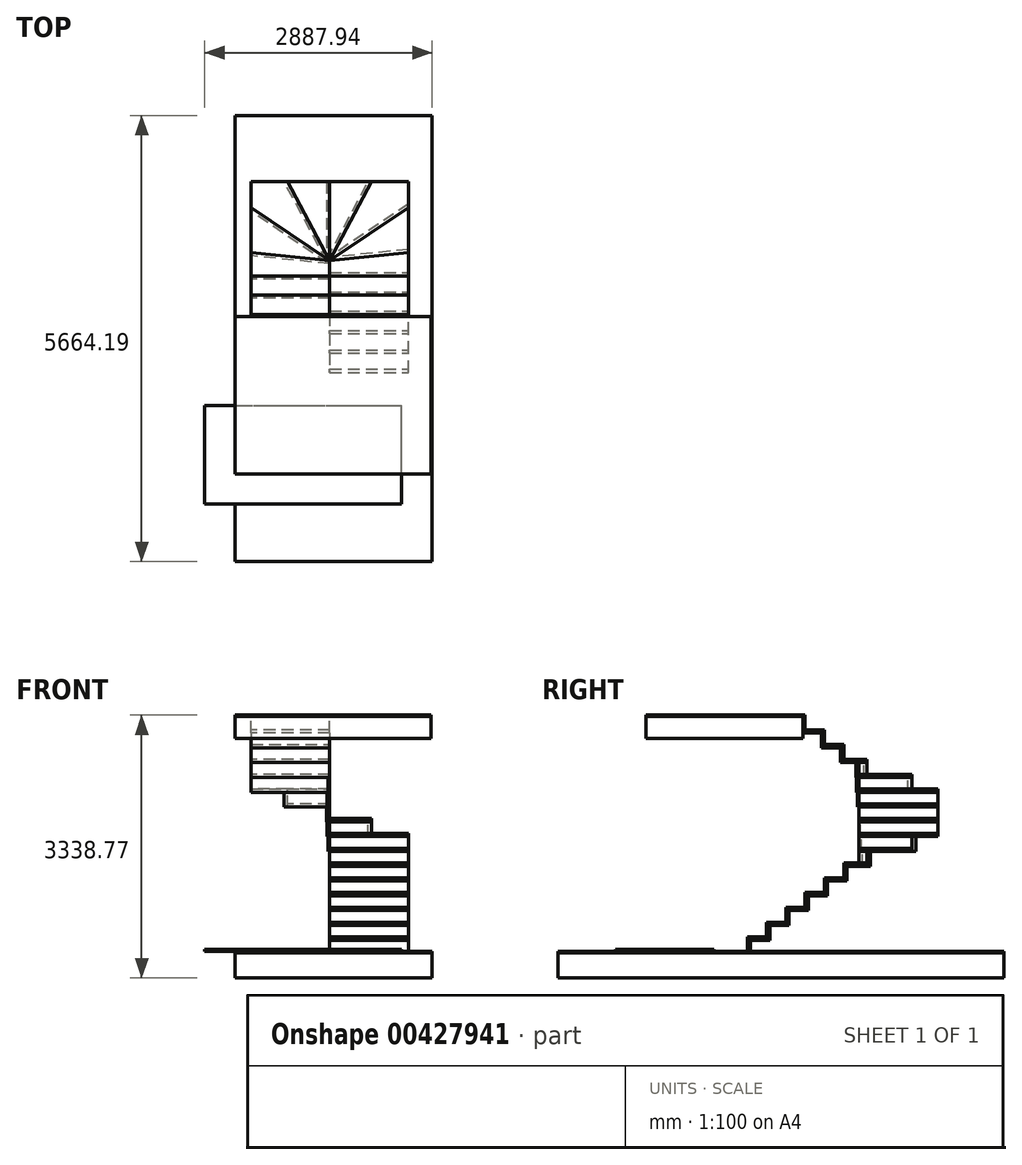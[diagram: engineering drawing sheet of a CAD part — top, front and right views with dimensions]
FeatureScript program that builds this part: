
annotation { "Feature Type Name" : "Feature", "Feature Type Description" : "" }
export const myFeature = defineFeature(function(context is Context, id is Id, definition is map)
    precondition{}
    {
        {
            assignVariable(context, id + "F0", {"name" : "up", "anyValue" : 188 - 40});
        }
        {
            assignVariable(context, id + "F1", {"name" : "height", "anyValue" : 188});
        }
        {
            var Q0;
            Q0=qCreatedBy(makeId("Top.planeOp"),FACE);
            var sketch = newSketch(context, id + "F2", { "sketchPlane" : qUnion([Q0])});
            skLineSegment(sketch, "E0.bottom", {"start": v(1000, 855) * mm, "end": v(-1000, 855) * mm, "construction": true});
            skLineSegment(sketch, "E0.top", {"start": v(1000, -855) * mm, "end": v(-1000, -855) * mm, "construction": true});
            skLineSegment(sketch, "E0.left", {"start": v(1000, 855) * mm, "end": v(1000, -855) * mm});
            skLineSegment(sketch, "E0.right", {"start": v(-1000, 855) * mm, "end": v(-1000, -855) * mm, "construction": true});
            skPoint(sketch, "E0.middle", {"position": v(0, 0) * mm});
            skLineSegment(sketch, "E1.bottom", {"start": v(-1000, -855) * mm, "end": v(0, -855) * mm, "construction": true});
            skLineSegment(sketch, "E1.top", {"start": v(-1000, 855) * mm, "end": v(0, 855) * mm, "construction": true});
            skLineSegment(sketch, "E1.left", {"start": v(-1000, -855) * mm, "end": v(-1000, 855) * mm});
            skLineSegment(sketch, "E1.right", {"start": v(0, -855) * mm, "end": v(0, 855) * mm});
            skLineSegment(sketch, "E2.bottom", {"start": v(1000, -855) * mm, "end": v(0, -855) * mm, "construction": true});
            skLineSegment(sketch, "E2.top", {"start": v(1000, 855) * mm, "end": v(0, 855) * mm});
            skLineSegment(sketch, "E2.left", {"start": v(1000, -855) * mm, "end": v(1000, 855) * mm});
            skLineSegment(sketch, "E3.bottom", {"start": v(-1000, 855) * mm, "end": v(1000, 855) * mm});
            skLineSegment(sketch, "E3.top", {"start": v(-1000, -145) * mm, "end": v(1000, -145) * mm, "construction": true});
            skLineSegment(sketch, "E3.left", {"start": v(-1000, 855) * mm, "end": v(-1000, -145) * mm, "construction": true});
            skLineSegment(sketch, "E3.right", {"start": v(1000, 855) * mm, "end": v(1000, -145) * mm, "construction": true});
            skCircle(sketch, "E4", {"center": v(0, -145) * mm, "radius": 1000 * mm, "construction": true});
            skArc(sketch, "E5", {"start": v(0, 355) * mm, "mid": v(-121.28, 340.07) * mm, "end": v(-235.31, 296.17) * mm, "construction": true});
            skArc(sketch, "E6", {"start": v(-235.31, 296.17) * mm, "mid": v(-335.3, 225.92) * mm, "end": v(-415.25, 133.51) * mm, "construction": true});
            skArc(sketch, "E7", {"start": v(-415.25, 133.51) * mm, "mid": v(-470.4, 24.47) * mm, "end": v(-497.46, -94.69) * mm, "construction": true});
            skArc(sketch, "E8", {"start": v(-497.46, -94.69) * mm, "mid": v(-499.37, -119.81) * mm, "end": v(-500, -145) * mm, "construction": true});
            skLineSegment(sketch, "E9", {"start": v(-500, -145) * mm, "end": v(-500, -855) * mm, "construction": true});
            skLineSegment(sketch, "E10", {"start": v(-1000, -340) * mm, "end": v(0, -340) * mm});
            skLineSegment(sketch, "E11", {"start": v(0, -585) * mm, "end": v(-1000, -585) * mm});
            skLineSegment(sketch, "E12", {"start": v(0, -830) * mm, "end": v(-1000, -830) * mm});
            skArc(sketch, "E13", {"start": v(0, 355) * mm, "mid": v(121.28, 340.07) * mm, "end": v(235.31, 296.17) * mm, "construction": true});
            skArc(sketch, "E14", {"start": v(235.31, 296.17) * mm, "mid": v(335.3, 225.92) * mm, "end": v(415.25, 133.51) * mm, "construction": true});
            skArc(sketch, "E15", {"start": v(415.25, 133.51) * mm, "mid": v(470.4, 24.47) * mm, "end": v(497.46, -94.69) * mm, "construction": true});
            skArc(sketch, "E16", {"start": v(497.46, -94.69) * mm, "mid": v(499.37, -119.81) * mm, "end": v(500, -145) * mm, "construction": true});
            skLineSegment(sketch, "E17", {"start": v(0, -340) * mm, "end": v(1000, -340) * mm});
            skLineSegment(sketch, "E18", {"start": v(0, -585) * mm, "end": v(1000, -585) * mm});
            skLineSegment(sketch, "E19", {"start": v(0, -830) * mm, "end": v(1000, -830) * mm});
            skLineSegment(sketch, "E20", {"start": v(0, -855) * mm, "end": v(0, -2275) * mm});
            skLineSegment(sketch, "E21", {"start": v(0, -2275) * mm, "end": v(1000, -2275) * mm});
            skLineSegment(sketch, "E22", {"start": v(1000, -2275) * mm, "end": v(1000, -855) * mm});
            skLineSegment(sketch, "E23", {"start": v(0, -145) * mm, "end": v(-497.46, -94.69) * mm});
            skLineSegment(sketch, "E24", {"start": v(-497.46, -94.69) * mm, "end": v(-1000, -43.86) * mm});
            skPoint(sketch, "E24.endSnap0", {"position": v(-1000, 0) * mm});
            skLineSegment(sketch, "E25", {"start": v(0, -145) * mm, "end": v(-415.25, 133.51) * mm});
            skLineSegment(sketch, "E26", {"start": v(-415.25, 133.51) * mm, "end": v(-1000, 525.7) * mm});
            skLineSegment(sketch, "E27", {"start": v(0, -145) * mm, "end": v(-235.31, 296.17) * mm});
            skLineSegment(sketch, "E28", {"start": v(-235.31, 296.17) * mm, "end": v(-533.39, 855) * mm});
            skLineSegment(sketch, "E29", {"start": v(0, -145) * mm, "end": v(235.31, 296.17) * mm});
            skLineSegment(sketch, "E30", {"start": v(235.31, 296.17) * mm, "end": v(533.39, 855) * mm});
            skLineSegment(sketch, "E31", {"start": v(0, -145) * mm, "end": v(415.25, 133.51) * mm});
            skLineSegment(sketch, "E32", {"start": v(415.25, 133.51) * mm, "end": v(1000, 525.7) * mm});
            skLineSegment(sketch, "E33", {"start": v(0, -145) * mm, "end": v(497.46, -94.69) * mm});
            skLineSegment(sketch, "E34", {"start": v(497.46, -94.69) * mm, "end": v(1000, -43.86) * mm});
            skLineSegment(sketch, "E35", {"start": v(0, -1075) * mm, "end": v(1000, -1075) * mm});
            skLineSegment(sketch, "E36", {"start": v(0, -1320) * mm, "end": v(1000, -1320) * mm});
            skLineSegment(sketch, "E37", {"start": v(0, -1565) * mm, "end": v(1000, -1565) * mm});
            skSolve(sketch);
        }
        {
            var Q0;
            Q0=qCreatedBy(makeId("Front.planeOp"),FACE);
            var Q1;
            Q1=sQuery(id+"F2.wireOp",VERTEX,"E1.right.start");
            cPlane(context, id + "F3", {"entities" : qUnion([Q0, Q1]), "cplaneType" : CPlaneType.PLANE_POINT, "offset" : 25 * mm, "width" : 150 * mm, "height" : 150 * mm});
        }
        {
            var Q0;
            Q0=qCreatedBy(id+"F3.planeOp",FACE);
            var sketch = newSketch(context, id + "F4", { "sketchPlane" : qUnion([Q0])});
            skLineSegment(sketch, "E38.bottom", {"start": v(-1199.88, 172) * mm, "end": v(1286.42, 172) * mm});
            skLineSegment(sketch, "E38.top", {"start": v(-1199.88, -108) * mm, "end": v(1286.42, -108) * mm});
            skLineSegment(sketch, "E38.left", {"start": v(-1199.88, 172) * mm, "end": v(-1199.88, -108) * mm});
            skLineSegment(sketch, "E38.right", {"start": v(1286.42, 172) * mm, "end": v(1286.42, -108) * mm});
            skSolve(sketch);
        }
        {
            var Q0;
            Q0 = qSketchRegion(id + "F4", true);
            extrude(context, id + "F5", {"entities" : qUnion([Q0]), "depth" : 2000 * mm});
        }
        {
            var Q0;
            Q0=makeQuery(id+"F5.opExtrude","SWEPT_FACE",FACE,{"disambiguationData":[OSD([sQuery(id+"F4.wireOp",EDGE,"E38.bottom")])]});
            extrude(context, id + "F6", {"entities" : qUnion([Q0]), "depth" : 16 * mm});
        }
        {
            var Q0;
            Q0=makeQuery(id+"F5.opExtrude","SWEPT_FACE",FACE,{"disambiguationData":[OSD([sQuery(id+"F4.wireOp",EDGE,"E38.left")])]});
            var sketch = newSketch(context, id + "F7", { "sketchPlane" : qUnion([Q0])});
            skLineSegment(sketch, "E39.bottom", {"start": v(3968.98, -3150.77) * mm, "end": v(-1695.2, -3150.77) * mm});
            skLineSegment(sketch, "E39.top", {"start": v(3968.98, -2833) * mm, "end": v(-1695.2, -2833) * mm});
            skLineSegment(sketch, "E39.left", {"start": v(3968.98, -3150.77) * mm, "end": v(3968.98, -2833) * mm});
            skLineSegment(sketch, "E39.right", {"start": v(-1695.2, -3150.77) * mm, "end": v(-1695.2, -2833) * mm});
            skLineSegment(sketch, "E40.0.0", {"start": v(855, 172) * mm, "end": v(855, -108) * mm});
            skLineSegment(sketch, "E40.0.1", {"start": v(855, -108) * mm, "end": v(2855, -108) * mm});
            skLineSegment(sketch, "E40.0.2", {"start": v(2855, -108) * mm, "end": v(2855, 172) * mm});
            skLineSegment(sketch, "E40.0.3", {"start": v(2855, 172) * mm, "end": v(855, 172) * mm});
            skSolve(sketch);
        }
        {
            var Q0;
            Q0=makeQuery(id+"F7.imprint","IMPRINT",FACE,{"disambiguationData":[TD([[makeQuery(id+"F7.imprint","IMPRINT",EDGE,{"derivedFrom":sQuery(id+"F7.wireOp",EDGE,"E39.bottom")}),-1.0]])]});
            extrude(context, id + "F8", {"entities" : qUnion([Q0]), "oppositeDirection" : true, "depth" : 2500 * mm});
        }
        {
            var Q0;
            Q0=makeQuery(id+"F8.opExtrude","SWEPT_FACE",FACE,{"disambiguationData":[OSD([sQuery(id+"F7.wireOp",EDGE,"E39.top")])]});
            extrude(context, id + "F9", {"entities" : qUnion([Q0]), "depth" : 16 * mm, "offsetDistance" : 25 * mm});
        }
        {
            var Q0;
            {var subQ0=sQuery(id+"F2.wireOp",EDGE,"E11");Q0=makeQuery(id+"F2.imprint","IMPRINT",FACE,{"disambiguationData":[TD([[makeQuery(id+"F2.imprint","IMPRINT",EDGE,{"derivedFrom":subQ0}),1.0]])]});}
            extrude(context, id + "F10", {"entities" : qUnion([Q0]), "oppositeDirection" : true, "depth" : 40 * mm});
        }
        {
            var Q0;
            Q0=makeQuery(id+"F10.opExtrude","CAP_FACE",FACE,{"disambiguationData":[OSD([sQuery(id+"F2.wireOp",EDGE,"E1.left"),sQuery(id+"F2.wireOp",EDGE,"E1.right"),sQuery(id+"F2.wireOp",EDGE,"E11"),sQuery(id+"F2.wireOp",EDGE,"E12")])],"isStart":false});
            cPlane(context, id + "F11", {"entities" : qUnion([Q0]), "cplaneType" : CPlaneType.OFFSET, "offset" : (getVariable(context, 'up')) * mm, "width" : 150 * mm, "height" : 150 * mm});
        }
        {
            var Q0;
            Q0=qCreatedBy(id+"F11.planeOp",FACE);
            var sketch = newSketch(context, id + "F12", { "sketchPlane" : qUnion([Q0])});
            skLineSegment(sketch, "E41.0.0", {"start": v(-1000, 585) * mm, "end": v(0, 585) * mm});
            skLineSegment(sketch, "E41.0.1", {"start": v(0, 585) * mm, "end": v(0, 340) * mm});
            skLineSegment(sketch, "E41.0.2", {"start": v(0, 340) * mm, "end": v(-1000, 340) * mm});
            skLineSegment(sketch, "E41.0.3", {"start": v(-1000, 340) * mm, "end": v(-1000, 585) * mm});
            skSolve(sketch);
        }
        {
            var Q0;
            Q0=makeQuery(id+"F12.imprint","IMPRINT",FACE,{"disambiguationData":[TD([[makeQuery(id+"F12.imprint","IMPRINT",EDGE,{"derivedFrom":sQuery(id+"F12.wireOp",EDGE,"E41.0.0")}),-1.0]])]});
            extrude(context, id + "F13", {"entities" : qUnion([Q0]), "depth" : 40 * mm});
        }
        {
            var Q0;
            Q0=makeQuery(id+"F13.opExtrude","CAP_FACE",FACE,{"disambiguationData":[OSD([sQuery(id+"F12.wireOp",EDGE,"E41.0.0"),sQuery(id+"F12.wireOp",EDGE,"E41.0.1"),sQuery(id+"F12.wireOp",EDGE,"E41.0.2"),sQuery(id+"F12.wireOp",EDGE,"E41.0.3")])],"isStart":false});
            cPlane(context, id + "F14", {"entities" : qUnion([Q0]), "cplaneType" : CPlaneType.OFFSET, "offset" : (getVariable(context, 'up')) * mm, "width" : 150 * mm, "height" : 150 * mm});
        }
        {
            var Q0;
            Q0=qCreatedBy(id+"F14.planeOp",FACE);
            var sketch = newSketch(context, id + "F15", { "sketchPlane" : qUnion([Q0])});
            skLineSegment(sketch, "E42.0.0", {"start": v(-1000, 43.86) * mm, "end": v(-1000, 340) * mm});
            skLineSegment(sketch, "E42.0.1", {"start": v(-1000, 340) * mm, "end": v(0, 340) * mm});
            skLineSegment(sketch, "E42.0.2", {"start": v(0, 340) * mm, "end": v(0, 145) * mm});
            skLineSegment(sketch, "E42.0.3", {"start": v(0, 145) * mm, "end": v(-497.46, 94.69) * mm});
            skLineSegment(sketch, "E42.0.4", {"start": v(-497.46, 94.69) * mm, "end": v(-1000, 43.86) * mm});
            skSolve(sketch);
        }
        {
            var Q0;
            Q0=makeQuery(id+"F15.imprint","IMPRINT",FACE,{"disambiguationData":[TD([[makeQuery(id+"F15.imprint","IMPRINT",EDGE,{"derivedFrom":sQuery(id+"F15.wireOp",EDGE,"E42.0.0")}),-1.0]])]});
            extrude(context, id + "F16", {"entities" : qUnion([Q0]), "depth" : 40 * mm});
        }
        {
            var Q0;
            Q0=makeQuery(id+"F16.opExtrude","CAP_FACE",FACE,{"disambiguationData":[OSD([sQuery(id+"F15.wireOp",EDGE,"E42.0.0"),sQuery(id+"F15.wireOp",EDGE,"E42.0.1"),sQuery(id+"F15.wireOp",EDGE,"E42.0.2"),sQuery(id+"F15.wireOp",EDGE,"E42.0.3"),sQuery(id+"F15.wireOp",EDGE,"E42.0.4")])],"isStart":false});
            cPlane(context, id + "F17", {"entities" : qUnion([Q0]), "cplaneType" : CPlaneType.OFFSET, "offset" : (getVariable(context, 'up')) * mm, "width" : 150 * mm, "height" : 150 * mm});
        }
        {
            var Q0;
            Q0=qCreatedBy(id+"F17.planeOp",FACE);
            var sketch = newSketch(context, id + "F18", { "sketchPlane" : qUnion([Q0])});
            skLineSegment(sketch, "E43.0.0", {"start": v(0, 145) * mm, "end": v(-415.25, -133.51) * mm});
            skLineSegment(sketch, "E43.0.1", {"start": v(-415.25, -133.51) * mm, "end": v(-1000, -525.7) * mm});
            skLineSegment(sketch, "E43.0.2", {"start": v(-1000, -525.7) * mm, "end": v(-1000, 43.86) * mm});
            skLineSegment(sketch, "E43.0.3", {"start": v(-1000, 43.86) * mm, "end": v(-497.46, 94.69) * mm});
            skLineSegment(sketch, "E43.0.4", {"start": v(-497.46, 94.69) * mm, "end": v(0, 145) * mm});
            skSolve(sketch);
        }
        {
            var Q0;
            Q0=makeQuery(id+"F18.imprint","IMPRINT",FACE,{"disambiguationData":[TD([[makeQuery(id+"F18.imprint","IMPRINT",EDGE,{"derivedFrom":sQuery(id+"F18.wireOp",EDGE,"E43.0.0")}),-1.0]])]});
            extrude(context, id + "F19", {"entities" : qUnion([Q0]), "depth" : 40 * mm});
        }
        {
            var Q0;
            Q0=makeQuery(id+"F19.opExtrude","CAP_FACE",FACE,{"disambiguationData":[OSD([sQuery(id+"F18.wireOp",EDGE,"E43.0.0"),sQuery(id+"F18.wireOp",EDGE,"E43.0.1"),sQuery(id+"F18.wireOp",EDGE,"E43.0.2"),sQuery(id+"F18.wireOp",EDGE,"E43.0.3"),sQuery(id+"F18.wireOp",EDGE,"E43.0.4")])],"isStart":false});
            cPlane(context, id + "F20", {"entities" : qUnion([Q0]), "cplaneType" : CPlaneType.OFFSET, "offset" : (getVariable(context, 'up')) * mm, "width" : 150 * mm, "height" : 150 * mm});
        }
        {
            var Q0;
            Q0=qCreatedBy(id+"F20.planeOp",FACE);
            var sketch = newSketch(context, id + "F21", { "sketchPlane" : qUnion([Q0])});
            skLineSegment(sketch, "E44.0.0", {"start": v(-1000, -525.7) * mm, "end": v(-415.25, -133.51) * mm});
            skLineSegment(sketch, "E44.0.1", {"start": v(-415.25, -133.51) * mm, "end": v(0, 145) * mm});
            skLineSegment(sketch, "E44.0.2", {"start": v(0, 145) * mm, "end": v(-235.31, -296.17) * mm});
            skLineSegment(sketch, "E44.0.3", {"start": v(-235.31, -296.17) * mm, "end": v(-533.39, -855) * mm});
            skLineSegment(sketch, "E44.0.4", {"start": v(-533.39, -855) * mm, "end": v(-1000, -855) * mm});
            skLineSegment(sketch, "E44.0.5", {"start": v(-1000, -855) * mm, "end": v(-1000, -525.7) * mm});
            skSolve(sketch);
        }
        {
            var Q0;
            Q0=makeQuery(id+"F21.imprint","IMPRINT",FACE,{"disambiguationData":[TD([[makeQuery(id+"F21.imprint","IMPRINT",EDGE,{"derivedFrom":sQuery(id+"F21.wireOp",EDGE,"E44.0.0")}),-1.0]])]});
            extrude(context, id + "F22", {"entities" : qUnion([Q0]), "depth" : 40 * mm});
        }
        {
            var Q0;
            Q0=makeQuery(id+"F22.opExtrude","CAP_FACE",FACE,{"disambiguationData":[OSD([sQuery(id+"F21.wireOp",EDGE,"E44.0.0"),sQuery(id+"F21.wireOp",EDGE,"E44.0.1"),sQuery(id+"F21.wireOp",EDGE,"E44.0.2"),sQuery(id+"F21.wireOp",EDGE,"E44.0.3"),sQuery(id+"F21.wireOp",EDGE,"E44.0.4"),sQuery(id+"F21.wireOp",EDGE,"E44.0.5")])],"isStart":false});
            cPlane(context, id + "F23", {"entities" : qUnion([Q0]), "cplaneType" : CPlaneType.OFFSET, "offset" : (getVariable(context, 'up')) * mm, "width" : 150 * mm, "height" : 150 * mm});
        }
        {
            var Q0;
            Q0=qCreatedBy(id+"F23.planeOp",FACE);
            var sketch = newSketch(context, id + "F24", { "sketchPlane" : qUnion([Q0])});
            skLineSegment(sketch, "E45.0.0", {"start": v(0, -855) * mm, "end": v(-533.39, -855) * mm});
            skLineSegment(sketch, "E45.0.1", {"start": v(-533.39, -855) * mm, "end": v(-235.31, -296.17) * mm});
            skLineSegment(sketch, "E45.0.2", {"start": v(-235.31, -296.17) * mm, "end": v(0, 145) * mm});
            skLineSegment(sketch, "E45.0.3", {"start": v(0, 145) * mm, "end": v(0, -855) * mm});
            skSolve(sketch);
        }
        {
            var Q0;
            Q0=makeQuery(id+"F24.imprint","IMPRINT",FACE,{"disambiguationData":[TD([[makeQuery(id+"F24.imprint","IMPRINT",EDGE,{"derivedFrom":sQuery(id+"F24.wireOp",EDGE,"E45.0.0")}),-1.0]])]});
            extrude(context, id + "F25", {"entities" : qUnion([Q0]), "depth" : 40 * mm});
        }
        {
            var Q0;
            Q0=makeQuery(id+"F25.opExtrude","CAP_FACE",FACE,{"disambiguationData":[OSD([sQuery(id+"F24.wireOp",EDGE,"E45.0.0"),sQuery(id+"F24.wireOp",EDGE,"E45.0.1"),sQuery(id+"F24.wireOp",EDGE,"E45.0.2"),sQuery(id+"F24.wireOp",EDGE,"E45.0.3")])],"isStart":false});
            cPlane(context, id + "F26", {"entities" : qUnion([Q0]), "cplaneType" : CPlaneType.OFFSET, "offset" : (getVariable(context, 'up')) * mm, "width" : 150 * mm, "height" : 150 * mm});
        }
        {
            var Q0;
            Q0=qCreatedBy(id+"F26.planeOp",FACE);
            var sketch = newSketch(context, id + "F27", { "sketchPlane" : qUnion([Q0])});
            skLineSegment(sketch, "E46.0.0", {"start": v(533.39, -855) * mm, "end": v(0, -855) * mm});
            skLineSegment(sketch, "E46.0.1", {"start": v(0, -855) * mm, "end": v(0, 145) * mm});
            skLineSegment(sketch, "E46.0.2", {"start": v(0, 145) * mm, "end": v(235.31, -296.17) * mm});
            skLineSegment(sketch, "E46.0.3", {"start": v(235.31, -296.17) * mm, "end": v(533.39, -855) * mm});
            skSolve(sketch);
        }
        {
            var Q0;
            Q0=makeQuery(id+"F27.imprint","IMPRINT",FACE,{"disambiguationData":[TD([[makeQuery(id+"F27.imprint","IMPRINT",EDGE,{"derivedFrom":sQuery(id+"F27.wireOp",EDGE,"E46.0.0")}),-1.0]])]});
            extrude(context, id + "F28", {"entities" : qUnion([Q0]), "depth" : 40 * mm});
        }
        {
            var Q0;
            Q0=makeQuery(id+"F28.opExtrude","CAP_FACE",FACE,{"disambiguationData":[OSD([sQuery(id+"F27.wireOp",EDGE,"E46.0.0"),sQuery(id+"F27.wireOp",EDGE,"E46.0.1"),sQuery(id+"F27.wireOp",EDGE,"E46.0.2"),sQuery(id+"F27.wireOp",EDGE,"E46.0.3")])],"isStart":false});
            cPlane(context, id + "F29", {"entities" : qUnion([Q0]), "cplaneType" : CPlaneType.OFFSET, "offset" : (getVariable(context, 'up')) * mm, "width" : 150 * mm, "height" : 150 * mm});
        }
        {
            var Q0;
            Q0=qCreatedBy(id+"F29.planeOp",FACE);
            var sketch = newSketch(context, id + "F30", { "sketchPlane" : qUnion([Q0])});
            skLineSegment(sketch, "E47.0.0", {"start": v(0, 145) * mm, "end": v(415.25, -133.51) * mm});
            skLineSegment(sketch, "E47.0.1", {"start": v(415.25, -133.51) * mm, "end": v(1000, -525.7) * mm});
            skLineSegment(sketch, "E47.0.2", {"start": v(1000, -525.7) * mm, "end": v(1000, -855) * mm});
            skLineSegment(sketch, "E47.0.3", {"start": v(1000, -855) * mm, "end": v(533.39, -855) * mm});
            skLineSegment(sketch, "E47.0.4", {"start": v(533.39, -855) * mm, "end": v(235.31, -296.17) * mm});
            skLineSegment(sketch, "E47.0.5", {"start": v(235.31, -296.17) * mm, "end": v(0, 145) * mm});
            skSolve(sketch);
        }
        {
            var Q0;
            Q0=makeQuery(id+"F30.imprint","IMPRINT",FACE,{"disambiguationData":[TD([[makeQuery(id+"F30.imprint","IMPRINT",EDGE,{"derivedFrom":sQuery(id+"F30.wireOp",EDGE,"E47.0.0")}),-1.0]])]});
            extrude(context, id + "F31", {"entities" : qUnion([Q0]), "depth" : 40 * mm});
        }
        {
            var Q0;
            Q0=makeQuery(id+"F31.opExtrude","CAP_FACE",FACE,{"disambiguationData":[OSD([sQuery(id+"F30.wireOp",EDGE,"E47.0.0"),sQuery(id+"F30.wireOp",EDGE,"E47.0.1"),sQuery(id+"F30.wireOp",EDGE,"E47.0.2"),sQuery(id+"F30.wireOp",EDGE,"E47.0.3"),sQuery(id+"F30.wireOp",EDGE,"E47.0.4"),sQuery(id+"F30.wireOp",EDGE,"E47.0.5")])],"isStart":false});
            cPlane(context, id + "F32", {"entities" : qUnion([Q0]), "cplaneType" : CPlaneType.OFFSET, "offset" : (getVariable(context, 'up')) * mm, "width" : 150 * mm, "height" : 150 * mm});
        }
        {
            var Q0;
            Q0=qCreatedBy(id+"F32.planeOp",FACE);
            var sketch = newSketch(context, id + "F33", { "sketchPlane" : qUnion([Q0])});
            skLineSegment(sketch, "E48.0.0", {"start": v(0, 145) * mm, "end": v(497.46, 94.69) * mm});
            skLineSegment(sketch, "E48.0.1", {"start": v(497.46, 94.69) * mm, "end": v(1000, 43.86) * mm});
            skLineSegment(sketch, "E48.0.2", {"start": v(1000, 43.86) * mm, "end": v(1000, -525.7) * mm});
            skLineSegment(sketch, "E48.0.3", {"start": v(1000, -525.7) * mm, "end": v(415.25, -133.51) * mm});
            skLineSegment(sketch, "E48.0.4", {"start": v(415.25, -133.51) * mm, "end": v(0, 145) * mm});
            skSolve(sketch);
        }
        {
            var Q0;
            Q0=makeQuery(id+"F33.imprint","IMPRINT",FACE,{"disambiguationData":[TD([[makeQuery(id+"F33.imprint","IMPRINT",EDGE,{"derivedFrom":sQuery(id+"F33.wireOp",EDGE,"E48.0.0")}),-1.0]])]});
            extrude(context, id + "F34", {"entities" : qUnion([Q0]), "depth" : 40 * mm});
        }
        {
            var Q0;
            Q0=makeQuery(id+"F34.opExtrude","CAP_FACE",FACE,{"disambiguationData":[OSD([sQuery(id+"F33.wireOp",EDGE,"E48.0.0"),sQuery(id+"F33.wireOp",EDGE,"E48.0.1"),sQuery(id+"F33.wireOp",EDGE,"E48.0.2"),sQuery(id+"F33.wireOp",EDGE,"E48.0.3"),sQuery(id+"F33.wireOp",EDGE,"E48.0.4")])],"isStart":false});
            cPlane(context, id + "F35", {"entities" : qUnion([Q0]), "cplaneType" : CPlaneType.OFFSET, "offset" : (getVariable(context, 'up')) * mm, "width" : 150 * mm, "height" : 150 * mm});
        }
        {
            var Q0;
            Q0=qCreatedBy(id+"F35.planeOp",FACE);
            var sketch = newSketch(context, id + "F36", { "sketchPlane" : qUnion([Q0])});
            skLineSegment(sketch, "E49.0.0", {"start": v(1000, 43.86) * mm, "end": v(497.46, 94.69) * mm});
            skLineSegment(sketch, "E49.0.1", {"start": v(497.46, 94.69) * mm, "end": v(0, 145) * mm});
            skLineSegment(sketch, "E49.0.2", {"start": v(0, 145) * mm, "end": v(0, 340) * mm});
            skLineSegment(sketch, "E49.0.3", {"start": v(0, 340) * mm, "end": v(1000, 340) * mm});
            skLineSegment(sketch, "E49.0.4", {"start": v(1000, 340) * mm, "end": v(1000, 43.86) * mm});
            skSolve(sketch);
        }
        {
            var Q0;
            Q0 = qSketchRegion(id + "F36", true);
            extrude(context, id + "F37", {"entities" : qUnion([Q0]), "depth" : 40 * mm});
        }
        {
            var Q0;
            Q0=makeQuery(id+"F37.opExtrude","CAP_FACE",FACE,{"disambiguationData":[OSD([sQuery(id+"F36.wireOp",EDGE,"E49.0.0"),sQuery(id+"F36.wireOp",EDGE,"E49.0.1"),sQuery(id+"F36.wireOp",EDGE,"E49.0.2"),sQuery(id+"F36.wireOp",EDGE,"E49.0.3"),sQuery(id+"F36.wireOp",EDGE,"E49.0.4")])],"isStart":false});
            cPlane(context, id + "F38", {"entities" : qUnion([Q0]), "cplaneType" : CPlaneType.OFFSET, "offset" : (getVariable(context, 'up')) * mm, "width" : 150 * mm, "height" : 150 * mm});
        }
        {
            var Q0;
            Q0=qCreatedBy(id+"F38.planeOp",FACE);
            var sketch = newSketch(context, id + "F39", { "sketchPlane" : qUnion([Q0])});
            skLineSegment(sketch, "E50.0.0", {"start": v(0, 340) * mm, "end": v(0, 585) * mm});
            skLineSegment(sketch, "E50.0.1", {"start": v(0, 585) * mm, "end": v(1000, 585) * mm});
            skLineSegment(sketch, "E50.0.2", {"start": v(1000, 585) * mm, "end": v(1000, 340) * mm});
            skLineSegment(sketch, "E50.0.3", {"start": v(1000, 340) * mm, "end": v(0, 340) * mm});
            skSolve(sketch);
        }
        {
            var Q0;
            Q0 = qSketchRegion(id + "F39", true);
            extrude(context, id + "F40", {"entities" : qUnion([Q0]), "depth" : 40 * mm});
        }
        {
            var Q0;
            Q0=makeQuery(id+"F40.opExtrude","CAP_FACE",FACE,{"disambiguationData":[OSD([sQuery(id+"F39.wireOp",EDGE,"E50.0.0"),sQuery(id+"F39.wireOp",EDGE,"E50.0.1"),sQuery(id+"F39.wireOp",EDGE,"E50.0.2"),sQuery(id+"F39.wireOp",EDGE,"E50.0.3")])],"isStart":false});
            cPlane(context, id + "F41", {"entities" : qUnion([Q0]), "cplaneType" : CPlaneType.OFFSET, "offset" : (getVariable(context, 'up')) * mm, "width" : 150 * mm, "height" : 150 * mm});
        }
        {
            var Q0;
            Q0=qCreatedBy(id+"F41.planeOp",FACE);
            var sketch = newSketch(context, id + "F42", { "sketchPlane" : qUnion([Q0])});
            skLineSegment(sketch, "E51.0.0", {"start": v(1000, 585) * mm, "end": v(0, 585) * mm});
            skLineSegment(sketch, "E51.0.1", {"start": v(0, 585) * mm, "end": v(0, 830) * mm});
            skLineSegment(sketch, "E51.0.2", {"start": v(0, 830) * mm, "end": v(1000, 830) * mm});
            skLineSegment(sketch, "E51.0.3", {"start": v(1000, 830) * mm, "end": v(1000, 585) * mm});
            skSolve(sketch);
        }
        {
            var Q0;
            Q0=makeQuery(id+"F42.imprint","IMPRINT",FACE,{"disambiguationData":[TD([[makeQuery(id+"F42.imprint","IMPRINT",EDGE,{"derivedFrom":sQuery(id+"F42.wireOp",EDGE,"E51.0.0")}),-1.0]])]});
            extrude(context, id + "F43", {"entities" : qUnion([Q0]), "depth" : 40 * mm});
        }
        {
            var Q0;
            Q0=makeQuery(id+"F43.opExtrude","CAP_FACE",FACE,{"disambiguationData":[OSD([sQuery(id+"F42.wireOp",EDGE,"E51.0.0"),sQuery(id+"F42.wireOp",EDGE,"E51.0.1"),sQuery(id+"F42.wireOp",EDGE,"E51.0.2"),sQuery(id+"F42.wireOp",EDGE,"E51.0.3")])],"isStart":false});
            cPlane(context, id + "F44", {"entities" : qUnion([Q0]), "cplaneType" : CPlaneType.OFFSET, "offset" : (getVariable(context, 'up')) * mm, "width" : 150 * mm, "height" : 150 * mm});
        }
        {
            var Q0;
            Q0=qCreatedBy(id+"F44.planeOp",FACE);
            var sketch = newSketch(context, id + "F45", { "sketchPlane" : qUnion([Q0])});
            skLineSegment(sketch, "E52.0.0", {"start": v(0, 855) * mm, "end": v(0, 1075) * mm});
            skLineSegment(sketch, "E52.0.1", {"start": v(0, 1075) * mm, "end": v(1000, 1075) * mm});
            skLineSegment(sketch, "E52.0.2", {"start": v(1000, 1075) * mm, "end": v(1000, 855) * mm});
            skLineSegment(sketch, "E52.0.3", {"start": v(1000, 855) * mm, "end": v(1000, 830) * mm});
            skLineSegment(sketch, "E52.0.4", {"start": v(1000, 830) * mm, "end": v(0, 830) * mm});
            skLineSegment(sketch, "E52.0.5", {"start": v(0, 830) * mm, "end": v(0, 855) * mm});
            skSolve(sketch);
        }
        {
            var Q0;
            Q0=makeQuery(id+"F45.imprint","IMPRINT",FACE,{"disambiguationData":[TD([[makeQuery(id+"F45.imprint","IMPRINT",EDGE,{"derivedFrom":sQuery(id+"F45.wireOp",EDGE,"E52.0.0")}),-1.0]])]});
            extrude(context, id + "F46", {"entities" : qUnion([Q0]), "depth" : 40 * mm});
        }
        {
            var Q0;
            Q0=makeQuery(id+"F46.opExtrude","CAP_FACE",FACE,{"disambiguationData":[OSD([sQuery(id+"F45.wireOp",EDGE,"E52.0.0"),sQuery(id+"F45.wireOp",EDGE,"E52.0.1"),sQuery(id+"F45.wireOp",EDGE,"E52.0.2"),sQuery(id+"F45.wireOp",EDGE,"E52.0.3"),sQuery(id+"F45.wireOp",EDGE,"E52.0.4"),sQuery(id+"F45.wireOp",EDGE,"E52.0.5")])],"isStart":false});
            cPlane(context, id + "F47", {"entities" : qUnion([Q0]), "cplaneType" : CPlaneType.OFFSET, "offset" : (getVariable(context, 'up')) * mm, "width" : 150 * mm, "height" : 150 * mm});
        }
        {
            var Q0;
            Q0=qCreatedBy(id+"F47.planeOp",FACE);
            var sketch = newSketch(context, id + "F48", { "sketchPlane" : qUnion([Q0])});
            skLineSegment(sketch, "E53.0.0", {"start": v(0, 1075) * mm, "end": v(0, 1320) * mm});
            skLineSegment(sketch, "E53.0.1", {"start": v(0, 1320) * mm, "end": v(1000, 1320) * mm});
            skLineSegment(sketch, "E53.0.2", {"start": v(1000, 1320) * mm, "end": v(1000, 1075) * mm});
            skLineSegment(sketch, "E53.0.3", {"start": v(1000, 1075) * mm, "end": v(0, 1075) * mm});
            skSolve(sketch);
        }
        {
            var Q0;
            Q0 = qSketchRegion(id + "F48", true);
            extrude(context, id + "F49", {"entities" : qUnion([Q0]), "depth" : 40 * mm});
        }
        {
            var Q0;
            Q0=makeQuery(id+"F49.opExtrude","CAP_FACE",FACE,{"disambiguationData":[OSD([sQuery(id+"F48.wireOp",EDGE,"E53.0.0"),sQuery(id+"F48.wireOp",EDGE,"E53.0.1"),sQuery(id+"F48.wireOp",EDGE,"E53.0.2"),sQuery(id+"F48.wireOp",EDGE,"E53.0.3")])],"isStart":false});
            cPlane(context, id + "F50", {"entities" : qUnion([Q0]), "cplaneType" : CPlaneType.OFFSET, "offset" : (getVariable(context, 'up')) * mm, "width" : 150 * mm, "height" : 150 * mm});
        }
        {
            var Q0;
            Q0=qCreatedBy(id+"F50.planeOp",FACE);
            var sketch = newSketch(context, id + "F51", { "sketchPlane" : qUnion([Q0])});
            skLineSegment(sketch, "E54.0.0", {"start": v(0, 1320) * mm, "end": v(0, 1565) * mm});
            skLineSegment(sketch, "E54.0.1", {"start": v(0, 1565) * mm, "end": v(1000, 1565) * mm});
            skLineSegment(sketch, "E54.0.2", {"start": v(1000, 1565) * mm, "end": v(1000, 1320) * mm});
            skLineSegment(sketch, "E54.0.3", {"start": v(1000, 1320) * mm, "end": v(0, 1320) * mm});
            skSolve(sketch);
        }
        {
            var Q0;
            Q0 = qSketchRegion(id + "F51", true);
            extrude(context, id + "F52", {"entities" : qUnion([Q0]), "depth" : 40 * mm});
        }
        {
            var Q0;
            Q0=makeQuery(id+"F10.opExtrude","SWEPT_FACE",FACE,{"disambiguationData":[OSD([sQuery(id+"F2.wireOp",EDGE,"E12")])]});
            var sketch = newSketch(context, id + "F53", { "sketchPlane" : qUnion([Q0])});
            skLineSegment(sketch, "E55.0.0", {"start": v(0, 0) * mm, "end": v(-1000, 0) * mm, "construction": true});
            skLineSegment(sketch, "E55.0.1", {"start": v(-1000, 0) * mm, "end": v(-1000, -40) * mm, "construction": true});
            skLineSegment(sketch, "E55.0.2", {"start": v(-1000, -40) * mm, "end": v(0, -40) * mm, "construction": true});
            skLineSegment(sketch, "E55.0.3", {"start": v(0, -40) * mm, "end": v(0, 0) * mm, "construction": true});
            skPoint(sketch, "E56.oppositeSnap0", {"position": v(0, -20) * mm});
            skLineSegment(sketch, "E56.bottom", {"start": v(-1000, -40) * mm, "end": v(0, -40) * mm});
            skLineSegment(sketch, "E56.top", {"start": v(-1000, 188) * mm, "end": v(0, 188) * mm});
            skLineSegment(sketch, "E56.left", {"start": v(-1000, -40) * mm, "end": v(-1000, 188) * mm});
            skLineSegment(sketch, "E56.right", {"start": v(0, -40) * mm, "end": v(0, 188) * mm});
            skSolve(sketch);
        }
        {
            var Q0;
            {var subQ0=sQuery(id+"F53.wireOp",EDGE,"E56.bottom");Q0=makeQuery(id+"F53.imprint","IMPRINT",FACE,{"disambiguationData":[TD([[makeQuery(id+"F53.imprint","IMPRINT",EDGE,{"derivedFrom":subQ0}),-1.0]])]});}
            var Q1;
            {var subQ0=sQuery(id+"F53.wireOp",EDGE,"E56.top");Q1=makeQuery(id+"F53.imprint","IMPRINT",FACE,{"disambiguationData":[TD([[makeQuery(id+"F53.imprint","IMPRINT",EDGE,{"derivedFrom":subQ0}),-1.0]])]});}
            extrude(context, id + "F54", {"entities" : qUnion([Q0, Q1]), "depth" : 25 * mm});
        }
        {
            var Q0;
            Q0=makeQuery(id+"F10.opExtrude","SWEPT_FACE",FACE,{"disambiguationData":[OSD([sQuery(id+"F2.wireOp",EDGE,"E1.left")])]});
            var sketch = newSketch(context, id + "F55", { "sketchPlane" : qUnion([Q0])});
            skLineSegment(sketch, "E57.bottom", {"start": v(585, -40) * mm, "end": v(625, -40) * mm});
            skLineSegment(sketch, "E57.top", {"start": v(585, -228) * mm, "end": v(625, -228) * mm});
            skLineSegment(sketch, "E57.left", {"start": v(585, -40) * mm, "end": v(585, -228) * mm});
            skLineSegment(sketch, "E57.right", {"start": v(625, -40) * mm, "end": v(625, -228) * mm});
            skSolve(sketch);
        }
        {
            var Q0;
            Q0=makeQuery(id+"F55.imprint","IMPRINT",FACE,{"disambiguationData":[TD([[makeQuery(id+"F55.imprint","IMPRINT",EDGE,{"derivedFrom":sQuery(id+"F55.wireOp",EDGE,"E57.bottom")}),1.0]])]});
            extrude(context, id + "F56", {"entities" : qUnion([Q0]), "oppositeDirection" : true, "depth" : 1000 * mm});
        }
        {
            var Q0;
            Q0=makeQuery(id+"F13.opExtrude","SWEPT_FACE",FACE,{"disambiguationData":[OSD([sQuery(id+"F12.wireOp",EDGE,"E41.0.3")])]});
            var sketch = newSketch(context, id + "F57", { "sketchPlane" : qUnion([Q0])});
            skLineSegment(sketch, "E58.bottom", {"start": v(340, -228) * mm, "end": v(380, -228) * mm});
            skLineSegment(sketch, "E58.top", {"start": v(340, -416) * mm, "end": v(380, -416) * mm});
            skLineSegment(sketch, "E58.left", {"start": v(340, -228) * mm, "end": v(340, -416) * mm});
            skLineSegment(sketch, "E58.right", {"start": v(380, -228) * mm, "end": v(380, -416) * mm});
            skSolve(sketch);
        }
        {
            var Q0;
            Q0=makeQuery(id+"F57.imprint","IMPRINT",FACE,{"disambiguationData":[TD([[makeQuery(id+"F57.imprint","IMPRINT",EDGE,{"derivedFrom":sQuery(id+"F57.wireOp",EDGE,"E58.bottom")}),-1.0]])]});
            extrude(context, id + "F58", {"entities" : qUnion([Q0]), "oppositeDirection" : true, "depth" : 1000 * mm});
        }
        {
            var Q0;
            Q0=makeQuery(id+"F16.opExtrude","CAP_FACE",FACE,{"disambiguationData":[OSD([sQuery(id+"F15.wireOp",EDGE,"E42.0.0"),sQuery(id+"F15.wireOp",EDGE,"E42.0.1"),sQuery(id+"F15.wireOp",EDGE,"E42.0.2"),sQuery(id+"F15.wireOp",EDGE,"E42.0.3"),sQuery(id+"F15.wireOp",EDGE,"E42.0.4")])],"isStart":false});
            var sketch = newSketch(context, id + "F59", { "sketchPlane" : qUnion([Q0])});
            skLineSegment(sketch, "E59.0.0", {"start": v(-1000, 43.86) * mm, "end": v(0, 145) * mm, "construction": true});
            skLineSegment(sketch, "E59.0.1", {"start": v(0, 145) * mm, "end": v(0, 340) * mm, "construction": true});
            skLineSegment(sketch, "E59.0.2", {"start": v(0, 340) * mm, "end": v(-1000, 340) * mm, "construction": true});
            skLineSegment(sketch, "E59.0.3", {"start": v(-1000, 340) * mm, "end": v(-1000, 43.86) * mm, "construction": true});
            skLineSegment(sketch, "E60", {"start": v(0, 145) * mm, "end": v(0, 185.2) * mm});
            skLineSegment(sketch, "E61", {"start": v(0, 185.2) * mm, "end": v(-1000, 84.06) * mm});
            skLineSegment(sketch, "E62", {"start": v(-1000, 84.06) * mm, "end": v(-1000, 43.86) * mm});
            skSolve(sketch);
        }
        {
            var Q0;
            {var subQ0=sQuery(id+"F59.wireOp",EDGE,"E60");Q0=makeQuery(id+"F59.imprint","IMPRINT",FACE,{"disambiguationData":[TD([[makeQuery(id+"F59.imprint","IMPRINT",EDGE,{"derivedFrom":subQ0}),-1.0]])]});}
            extrude(context, id + "F60", {"entities" : qUnion([Q0]), "depth" : (getVariable(context, 'height')) * mm});
        }
        {
            var Q0;
            Q0=makeQuery(id+"F19.opExtrude","CAP_FACE",FACE,{"disambiguationData":[OSD([sQuery(id+"F18.wireOp",EDGE,"E43.0.0"),sQuery(id+"F18.wireOp",EDGE,"E43.0.1"),sQuery(id+"F18.wireOp",EDGE,"E43.0.2"),sQuery(id+"F18.wireOp",EDGE,"E43.0.3"),sQuery(id+"F18.wireOp",EDGE,"E43.0.4")])],"isStart":false});
            var sketch = newSketch(context, id + "F61", { "sketchPlane" : qUnion([Q0])});
            skLineSegment(sketch, "E63.0.0", {"start": v(0, 145) * mm, "end": v(-1000, 43.86) * mm, "construction": true});
            skLineSegment(sketch, "E63.0.1", {"start": v(-1000, 43.86) * mm, "end": v(-1000, -525.7) * mm, "construction": true});
            skLineSegment(sketch, "E63.0.2", {"start": v(-1000, -525.7) * mm, "end": v(0, 145) * mm, "construction": true});
            skLineSegment(sketch, "E64", {"start": v(0, 145) * mm, "end": v(-22.28, 178.22) * mm});
            skLineSegment(sketch, "E65", {"start": v(-22.28, 178.22) * mm, "end": v(-1000, -477.55) * mm});
            skLineSegment(sketch, "E66", {"start": v(-1000, -477.55) * mm, "end": v(-1000, -525.7) * mm});
            skLineSegment(sketch, "E67", {"start": v(-1000, -525.7) * mm, "end": v(0, 145) * mm});
            skSolve(sketch);
        }
        {
            var Q0;
            {var subQ0=sQuery(id+"F61.wireOp",EDGE,"E66");Q0=makeQuery(id+"F61.imprint","IMPRINT",FACE,{"disambiguationData":[TD([[makeQuery(id+"F61.imprint","IMPRINT",EDGE,{"derivedFrom":subQ0}),-1.0]])]});}
            var Q1;
            {var subQ0=sQuery(id+"F61.wireOp",EDGE,"E64");Q1=makeQuery(id+"F61.imprint","IMPRINT",FACE,{"disambiguationData":[TD([[makeQuery(id+"F61.imprint","IMPRINT",EDGE,{"derivedFrom":subQ0}),1.0]])]});}
            extrude(context, id + "F62", {"entities" : qUnion([Q0, Q1]), "depth" : (getVariable(context, 'height')) * mm});
        }
        {
            var Q0;
            Q0=makeQuery(id+"F22.opExtrude","CAP_FACE",FACE,{"disambiguationData":[OSD([sQuery(id+"F21.wireOp",EDGE,"E44.0.0"),sQuery(id+"F21.wireOp",EDGE,"E44.0.1"),sQuery(id+"F21.wireOp",EDGE,"E44.0.2"),sQuery(id+"F21.wireOp",EDGE,"E44.0.3"),sQuery(id+"F21.wireOp",EDGE,"E44.0.4"),sQuery(id+"F21.wireOp",EDGE,"E44.0.5")])],"isStart":false});
            var sketch = newSketch(context, id + "F63", { "sketchPlane" : qUnion([Q0])});
            skLineSegment(sketch, "E68.0.0", {"start": v(-1000, -525.7) * mm, "end": v(-1000, -855) * mm, "construction": true});
            skLineSegment(sketch, "E68.0.1", {"start": v(-1000, -855) * mm, "end": v(-533.39, -855) * mm, "construction": true});
            skLineSegment(sketch, "E68.0.2", {"start": v(-533.39, -855) * mm, "end": v(0, 145) * mm, "construction": true});
            skLineSegment(sketch, "E68.0.3", {"start": v(0, 145) * mm, "end": v(-1000, -525.7) * mm, "construction": true});
            skLineSegment(sketch, "E69", {"start": v(0, 145) * mm, "end": v(-35.3, 163.83) * mm});
            skLineSegment(sketch, "E70", {"start": v(-35.3, 163.83) * mm, "end": v(-578.72, -855) * mm});
            skLineSegment(sketch, "E71", {"start": v(-578.72, -855) * mm, "end": v(-533.39, -855) * mm});
            skLineSegment(sketch, "E72", {"start": v(0, 145) * mm, "end": v(-533.39, -855) * mm});
            skSolve(sketch);
        }
        {
            var Q0;
            {var subQ0=sQuery(id+"F63.wireOp",EDGE,"E71");Q0=makeQuery(id+"F63.imprint","IMPRINT",FACE,{"disambiguationData":[TD([[makeQuery(id+"F63.imprint","IMPRINT",EDGE,{"derivedFrom":subQ0}),-1.0]])]});}
            var Q1;
            {var subQ0=sQuery(id+"F63.wireOp",EDGE,"E69");Q1=makeQuery(id+"F63.imprint","IMPRINT",FACE,{"disambiguationData":[TD([[makeQuery(id+"F63.imprint","IMPRINT",EDGE,{"derivedFrom":subQ0}),1.0]])]});}
            extrude(context, id + "F64", {"entities" : qUnion([Q0, Q1]), "depth" : (getVariable(context, 'height')) * mm});
        }
        {
            var Q0;
            Q0=makeQuery(id+"F25.opExtrude","CAP_FACE",FACE,{"disambiguationData":[OSD([sQuery(id+"F24.wireOp",EDGE,"E45.0.0"),sQuery(id+"F24.wireOp",EDGE,"E45.0.1"),sQuery(id+"F24.wireOp",EDGE,"E45.0.2"),sQuery(id+"F24.wireOp",EDGE,"E45.0.3")])],"isStart":false});
            var sketch = newSketch(context, id + "F65", { "sketchPlane" : qUnion([Q0])});
            skLineSegment(sketch, "E73.0.0", {"start": v(0, -855) * mm, "end": v(0, 145) * mm, "construction": true});
            skLineSegment(sketch, "E73.0.1", {"start": v(0, 145) * mm, "end": v(-533.39, -855) * mm, "construction": true});
            skLineSegment(sketch, "E73.0.2", {"start": v(-533.39, -855) * mm, "end": v(0, -855) * mm, "construction": true});
            skLineSegment(sketch, "E74", {"start": v(0, -855) * mm, "end": v(-40, -855) * mm});
            skLineSegment(sketch, "E75", {"start": v(-40, -855) * mm, "end": v(-40, 145) * mm});
            skLineSegment(sketch, "E76", {"start": v(-40, 145) * mm, "end": v(0, 145) * mm});
            skLineSegment(sketch, "E77", {"start": v(0, -855) * mm, "end": v(0, 145) * mm});
            skSolve(sketch);
        }
        {
            var Q0;
            Q0 = qSketchRegion(id + "F65", true);
            extrude(context, id + "F66", {"entities" : qUnion([Q0]), "depth" : (getVariable(context, 'height')) * mm});
        }
        {
            var Q0;
            Q0=makeQuery(id+"F28.opExtrude","CAP_FACE",FACE,{"disambiguationData":[OSD([sQuery(id+"F27.wireOp",EDGE,"E46.0.0"),sQuery(id+"F27.wireOp",EDGE,"E46.0.1"),sQuery(id+"F27.wireOp",EDGE,"E46.0.2"),sQuery(id+"F27.wireOp",EDGE,"E46.0.3")])],"isStart":false});
            var sketch = newSketch(context, id + "F67", { "sketchPlane" : qUnion([Q0])});
            skLineSegment(sketch, "E78.0.0", {"start": v(533.39, -855) * mm, "end": v(0, 145) * mm, "construction": true});
            skLineSegment(sketch, "E78.0.1", {"start": v(0, 145) * mm, "end": v(0, -855) * mm, "construction": true});
            skLineSegment(sketch, "E78.0.2", {"start": v(0, -855) * mm, "end": v(533.39, -855) * mm, "construction": true});
            skLineSegment(sketch, "E79", {"start": v(0, 145) * mm, "end": v(-35.3, 126.17) * mm});
            skLineSegment(sketch, "E80", {"start": v(-35.3, 126.17) * mm, "end": v(488.05, -855) * mm});
            skLineSegment(sketch, "E81", {"start": v(488.05, -855) * mm, "end": v(533.39, -855) * mm});
            skLineSegment(sketch, "E82", {"start": v(533.39, -855) * mm, "end": v(0, 145) * mm});
            skSolve(sketch);
        }
        {
            var Q0;
            Q0 = qSketchRegion(id + "F67", true);
            extrude(context, id + "F68", {"entities" : qUnion([Q0]), "depth" : (getVariable(context, 'height')) * mm});
        }
        {
            var Q0;
            Q0=makeQuery(id+"F31.opExtrude","CAP_FACE",FACE,{"disambiguationData":[OSD([sQuery(id+"F30.wireOp",EDGE,"E47.0.0"),sQuery(id+"F30.wireOp",EDGE,"E47.0.1"),sQuery(id+"F30.wireOp",EDGE,"E47.0.2"),sQuery(id+"F30.wireOp",EDGE,"E47.0.3"),sQuery(id+"F30.wireOp",EDGE,"E47.0.4"),sQuery(id+"F30.wireOp",EDGE,"E47.0.5")])],"isStart":false});
            var sketch = newSketch(context, id + "F69", { "sketchPlane" : qUnion([Q0])});
            skLineSegment(sketch, "E83.0.0", {"start": v(0, 145) * mm, "end": v(533.39, -855) * mm, "construction": true});
            skLineSegment(sketch, "E83.0.1", {"start": v(533.39, -855) * mm, "end": v(1000, -855) * mm, "construction": true});
            skLineSegment(sketch, "E83.0.2", {"start": v(1000, -855) * mm, "end": v(1000, -525.7) * mm, "construction": true});
            skLineSegment(sketch, "E83.0.3", {"start": v(1000, -525.7) * mm, "end": v(0, 145) * mm, "construction": true});
            skLineSegment(sketch, "E84", {"start": v(1000, -525.7) * mm, "end": v(1000, -573.87) * mm});
            skLineSegment(sketch, "E85", {"start": v(1000, -573.87) * mm, "end": v(-22.28, 111.78) * mm});
            skLineSegment(sketch, "E86", {"start": v(-22.28, 111.78) * mm, "end": v(0, 145) * mm});
            skLineSegment(sketch, "E87", {"start": v(0, 145) * mm, "end": v(1000, -525.7) * mm});
            skSolve(sketch);
        }
        {
            var Q0;
            Q0 = qSketchRegion(id + "F69", true);
            extrude(context, id + "F70", {"entities" : qUnion([Q0]), "depth" : (getVariable(context, 'height')) * mm});
        }
        {
            var Q0;
            Q0=makeQuery(id+"F34.opExtrude","CAP_FACE",FACE,{"disambiguationData":[OSD([sQuery(id+"F33.wireOp",EDGE,"E48.0.0"),sQuery(id+"F33.wireOp",EDGE,"E48.0.1"),sQuery(id+"F33.wireOp",EDGE,"E48.0.2"),sQuery(id+"F33.wireOp",EDGE,"E48.0.3"),sQuery(id+"F33.wireOp",EDGE,"E48.0.4")])],"isStart":false});
            var sketch = newSketch(context, id + "F71", { "sketchPlane" : qUnion([Q0])});
            skLineSegment(sketch, "E88.0.0", {"start": v(0, 145) * mm, "end": v(1000, -525.7) * mm, "construction": true});
            skLineSegment(sketch, "E88.0.1", {"start": v(1000, -525.7) * mm, "end": v(1000, 43.86) * mm, "construction": true});
            skLineSegment(sketch, "E88.0.2", {"start": v(1000, 43.86) * mm, "end": v(0, 145) * mm, "construction": true});
            skLineSegment(sketch, "E89", {"start": v(1000, 43.86) * mm, "end": v(1000, 3.66) * mm});
            skLineSegment(sketch, "E90", {"start": v(1000, 3.66) * mm, "end": v(-4.03, 105.2) * mm});
            skLineSegment(sketch, "E91", {"start": v(-4.03, 105.2) * mm, "end": v(0, 145) * mm});
            skLineSegment(sketch, "E92", {"start": v(0, 145) * mm, "end": v(1000, 43.86) * mm});
            skSolve(sketch);
        }
        {
            var Q0;
            Q0 = qSketchRegion(id + "F71", true);
            extrude(context, id + "F72", {"entities" : qUnion([Q0]), "depth" : (getVariable(context, 'height')) * mm});
        }
        {
            var Q0;
            Q0=makeQuery(id+"F37.opExtrude","SWEPT_FACE",FACE,{"disambiguationData":[OSD([sQuery(id+"F36.wireOp",EDGE,"E49.0.4")])]});
            var sketch = newSketch(context, id + "F73", { "sketchPlane" : qUnion([Q0])});
            skLineSegment(sketch, "E93.0.0", {"start": v(-43.86, -1692) * mm, "end": v(-340, -1692) * mm, "construction": true});
            skLineSegment(sketch, "E93.0.1", {"start": v(-340, -1692) * mm, "end": v(-340, -1732) * mm, "construction": true});
            skLineSegment(sketch, "E93.0.2", {"start": v(-340, -1732) * mm, "end": v(-43.86, -1732) * mm, "construction": true});
            skLineSegment(sketch, "E93.0.3", {"start": v(-43.86, -1732) * mm, "end": v(-43.86, -1692) * mm, "construction": true});
            skLineSegment(sketch, "E94.0.0", {"start": v(-340, -1880) * mm, "end": v(-585, -1880) * mm, "construction": true});
            skLineSegment(sketch, "E94.0.1", {"start": v(-585, -1880) * mm, "end": v(-585, -1920) * mm, "construction": true});
            skLineSegment(sketch, "E94.0.2", {"start": v(-585, -1920) * mm, "end": v(-340, -1920) * mm, "construction": true});
            skLineSegment(sketch, "E94.0.3", {"start": v(-340, -1920) * mm, "end": v(-340, -1880) * mm, "construction": true});
            skLineSegment(sketch, "E95.0.0", {"start": v(-585, -2068) * mm, "end": v(-830, -2068) * mm, "construction": true});
            skLineSegment(sketch, "E95.0.1", {"start": v(-830, -2068) * mm, "end": v(-830, -2108) * mm, "construction": true});
            skLineSegment(sketch, "E95.0.2", {"start": v(-830, -2108) * mm, "end": v(-585, -2108) * mm, "construction": true});
            skLineSegment(sketch, "E95.0.3", {"start": v(-585, -2108) * mm, "end": v(-585, -2068) * mm, "construction": true});
            skLineSegment(sketch, "E96.0.0", {"start": v(-830, -2256) * mm, "end": v(-1075, -2256) * mm, "construction": true});
            skLineSegment(sketch, "E96.0.1", {"start": v(-1075, -2256) * mm, "end": v(-1075, -2296) * mm, "construction": true});
            skLineSegment(sketch, "E96.0.2", {"start": v(-1075, -2296) * mm, "end": v(-830, -2296) * mm, "construction": true});
            skLineSegment(sketch, "E96.0.3", {"start": v(-830, -2296) * mm, "end": v(-830, -2256) * mm, "construction": true});
            skLineSegment(sketch, "E97.0.0", {"start": v(-1075, -2444) * mm, "end": v(-1320, -2444) * mm, "construction": true});
            skLineSegment(sketch, "E97.0.1", {"start": v(-1320, -2444) * mm, "end": v(-1320, -2484) * mm, "construction": true});
            skLineSegment(sketch, "E97.0.2", {"start": v(-1320, -2484) * mm, "end": v(-1075, -2484) * mm, "construction": true});
            skLineSegment(sketch, "E97.0.3", {"start": v(-1075, -2484) * mm, "end": v(-1075, -2444) * mm, "construction": true});
            skLineSegment(sketch, "E98.0.0", {"start": v(-1320, -2632) * mm, "end": v(-1565, -2632) * mm, "construction": true});
            skLineSegment(sketch, "E98.0.1", {"start": v(-1565, -2632) * mm, "end": v(-1565, -2672) * mm, "construction": true});
            skLineSegment(sketch, "E98.0.2", {"start": v(-1565, -2672) * mm, "end": v(-1320, -2672) * mm, "construction": true});
            skLineSegment(sketch, "E98.0.3", {"start": v(-1320, -2672) * mm, "end": v(-1320, -2632) * mm, "construction": true});
            skLineSegment(sketch, "E99.bottom", {"start": v(-340, -1732) * mm, "end": v(-300, -1732) * mm, "construction": true});
            skLineSegment(sketch, "E99.top", {"start": v(-340, -1920) * mm, "end": v(-300, -1920) * mm});
            skLineSegment(sketch, "E99.left", {"start": v(-340, -1732) * mm, "end": v(-340, -1920) * mm});
            skLineSegment(sketch, "E99.right", {"start": v(-300, -1732) * mm, "end": v(-300, -1920) * mm});
            skLineSegment(sketch, "E100.bottom", {"start": v(-585, -1920) * mm, "end": v(-545, -1920) * mm});
            skLineSegment(sketch, "E100.top", {"start": v(-585, -2108) * mm, "end": v(-545, -2108) * mm});
            skLineSegment(sketch, "E100.left", {"start": v(-585, -1920) * mm, "end": v(-585, -2108) * mm});
            skLineSegment(sketch, "E100.right", {"start": v(-545, -1920) * mm, "end": v(-545, -2108) * mm});
            skLineSegment(sketch, "E101.bottom", {"start": v(-830, -2108) * mm, "end": v(-790, -2108) * mm});
            skLineSegment(sketch, "E101.top", {"start": v(-830, -2296) * mm, "end": v(-790, -2296) * mm});
            skLineSegment(sketch, "E101.left", {"start": v(-830, -2108) * mm, "end": v(-830, -2296) * mm});
            skLineSegment(sketch, "E101.right", {"start": v(-790, -2108) * mm, "end": v(-790, -2296) * mm});
            skLineSegment(sketch, "E102.bottom", {"start": v(-1075, -2296) * mm, "end": v(-1035, -2296) * mm});
            skLineSegment(sketch, "E102.top", {"start": v(-1075, -2484) * mm, "end": v(-1035, -2484) * mm});
            skLineSegment(sketch, "E102.left", {"start": v(-1075, -2296) * mm, "end": v(-1075, -2484) * mm});
            skLineSegment(sketch, "E102.right", {"start": v(-1035, -2296) * mm, "end": v(-1035, -2484) * mm});
            skLineSegment(sketch, "E103.bottom", {"start": v(-1320, -2484) * mm, "end": v(-1280, -2484) * mm});
            skLineSegment(sketch, "E103.top", {"start": v(-1320, -2672) * mm, "end": v(-1280, -2672) * mm});
            skLineSegment(sketch, "E103.left", {"start": v(-1320, -2484) * mm, "end": v(-1320, -2672) * mm});
            skLineSegment(sketch, "E103.right", {"start": v(-1280, -2484) * mm, "end": v(-1280, -2672) * mm});
            skLineSegment(sketch, "E104.0.0", {"start": v(-3968.98, -2833) * mm, "end": v(1695.2, -2833) * mm, "construction": true});
            skLineSegment(sketch, "E104.0.1", {"start": v(1695.2, -2833) * mm, "end": v(1695.2, -2817) * mm, "construction": true});
            skLineSegment(sketch, "E104.0.2", {"start": v(1695.2, -2817) * mm, "end": v(-3968.98, -2817) * mm, "construction": true});
            skLineSegment(sketch, "E104.0.3", {"start": v(-3968.98, -2817) * mm, "end": v(-3968.98, -2833) * mm, "construction": true});
            skLineSegment(sketch, "E105.bottom", {"start": v(-1565, -2672) * mm, "end": v(-1525, -2672) * mm});
            skLineSegment(sketch, "E105.top", {"start": v(-1565, -2817) * mm, "end": v(-1525, -2817) * mm});
            skLineSegment(sketch, "E105.left", {"start": v(-1565, -2672) * mm, "end": v(-1565, -2817) * mm});
            skLineSegment(sketch, "E105.right", {"start": v(-1525, -2672) * mm, "end": v(-1525, -2817) * mm});
            skSolve(sketch);
        }
        {
            var Q0;
            Q0 = qSketchRegion(id + "F73", true);
            var Q1;
            Q1=makeQuery(id+"F73.imprint","IMPRINT",FACE,{"disambiguationData":[TD([[makeQuery(id+"F73.imprint","IMPRINT",EDGE,{"derivedFrom":sQuery(id+"F73.wireOp",EDGE,"E99.top")}),1.0]])]});
            extrude(context, id + "F74", {"entities" : qUnion([Q0, Q1]), "oppositeDirection" : true, "depth" : 1000 * mm});
        }
        {
            var Q0;
            Q0=makeQuery(id+"F9.opExtrude","CAP_FACE",FACE,{"disambiguationData":[OSD([sQuery(id+"F7.wireOp",EDGE,"E39.top")])],"isStart":false});
            var sketch = newSketch(context, id + "F75", { "sketchPlane" : qUnion([Q0])});
            skLineSegment(sketch, "E106.bottom", {"start": v(-1587.82, -3238.9) * mm, "end": v(912.18, -3238.9) * mm});
            skLineSegment(sketch, "E106.top", {"start": v(-1587.82, -1988.9) * mm, "end": v(912.18, -1988.9) * mm});
            skLineSegment(sketch, "E106.left", {"start": v(-1587.82, -3238.9) * mm, "end": v(-1587.82, -1988.9) * mm});
            skLineSegment(sketch, "E106.right", {"start": v(912.18, -3238.9) * mm, "end": v(912.18, -1988.9) * mm});
            skPoint(sketch, "E106.middle", {"position": v(-337.82, -2613.9) * mm});
            skSolve(sketch);
        }
        {
            var Q0;
            Q0 = qSketchRegion(id + "F75", true);
            extrude(context, id + "F76", {"entities" : qUnion([Q0]), "depth" : 28 * mm, "offsetDistance" : 25 * mm});
        }
    });
